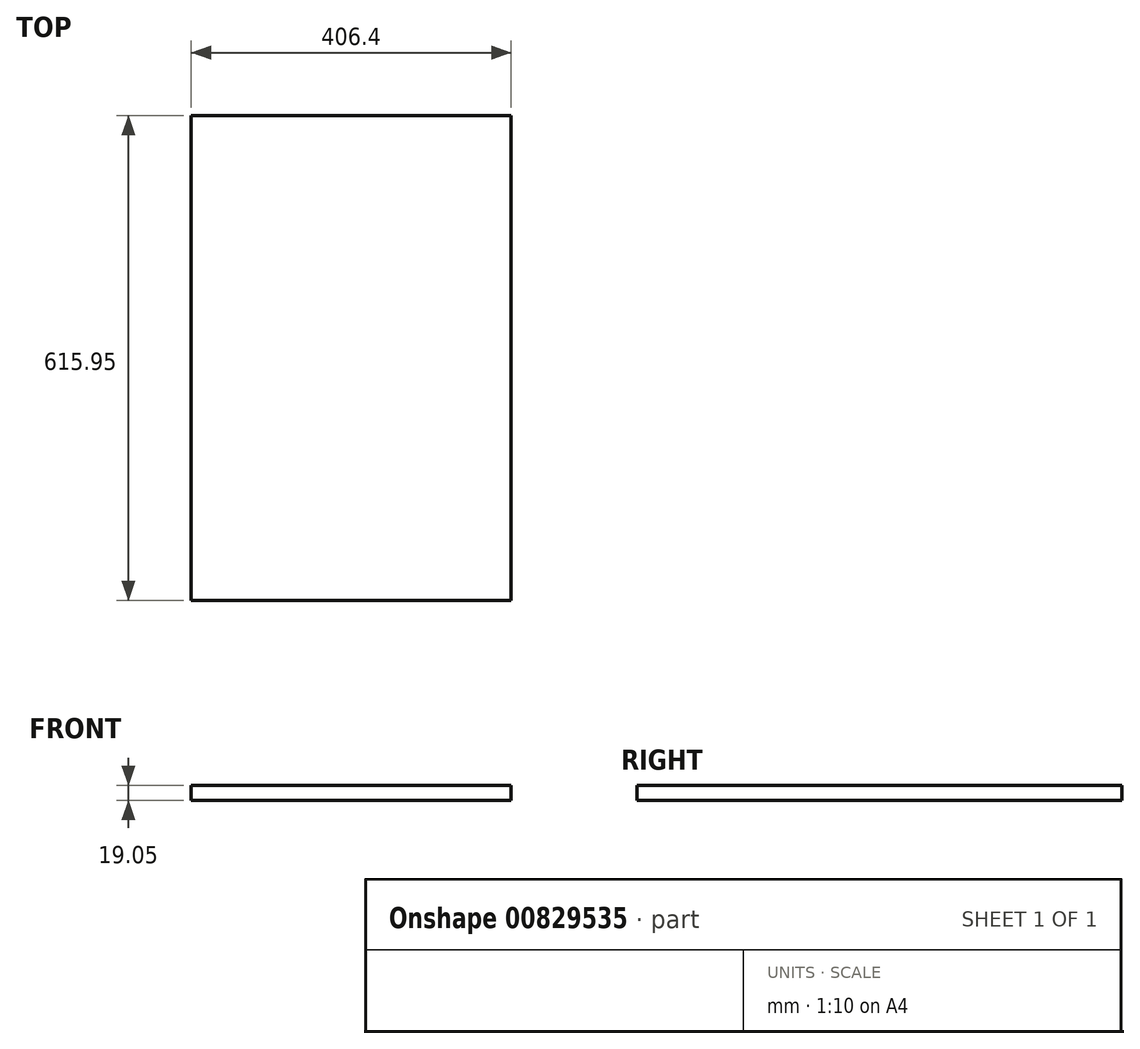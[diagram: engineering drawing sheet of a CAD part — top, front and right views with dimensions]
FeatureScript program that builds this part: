
annotation { "Feature Type Name" : "Feature", "Feature Type Description" : "" }
export const myFeature = defineFeature(function(context is Context, id is Id, definition is map)
    precondition{}
    {
        {
            var Q0;
            Q0=qCreatedBy(makeId("Front.planeOp"),FACE);
            var sketch = newSketch(context, id + "F0", { "sketchPlane" : qUnion([Q0])});
            skLineSegment(sketch, "E0.bottom", {"start": v(0, 0) * mm, "end": v(406.4, 0) * mm});
            skLineSegment(sketch, "E0.top", {"start": v(0, 19.05) * mm, "end": v(406.4, 19.05) * mm});
            skLineSegment(sketch, "E0.left", {"start": v(0, 0) * mm, "end": v(0, 19.05) * mm});
            skLineSegment(sketch, "E0.right", {"start": v(406.4, 0) * mm, "end": v(406.4, 19.05) * mm});
            skSolve(sketch);
        }
        {
            var Q0;
            Q0=makeQuery(id+"F0.imprint","IMPRINT",FACE,{"disambiguationData":[TD([[makeQuery(id+"F0.imprint","IMPRINT",EDGE,{"derivedFrom":sQuery(id+"F0.wireOp",EDGE,"E0.bottom")}),1.0]])]});
            extrude(context, id + "F1", {"entities" : qUnion([Q0]), "depth" : 615.95 * mm, "offsetDistance" : 25.4 * mm});
        }
    });
